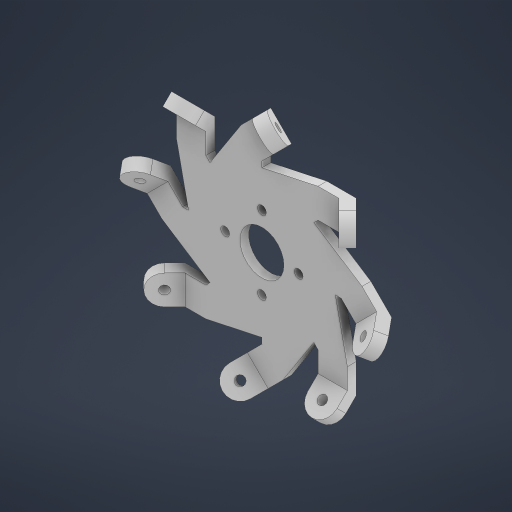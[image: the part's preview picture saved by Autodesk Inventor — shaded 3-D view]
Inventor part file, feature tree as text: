
AUTODESK INVENTOR PART (.ipt)
format: ipt  version: 2023 (Build 270158000, 158)  size: 317,952 bytes
history: native  units: mm
features: extrude x3, sketch x3, plane x1, fillet x1, pattern_circular x1
ambient origin geometry x8: Origin, YZ Plane, XZ Plane, XY Plane, X Axis, Y Axis, Z Axis, Center Point
bodies: Solid1 (feature_tree)
feature tree (9):
  extrude  "Extrusion1"  Depth=50.0mm
  plane  "Work Plane1"
  extrude  "Extrusion2"  Depth=10.0mm
  fillet  "Fillet1"  [1 undecoded]
  extrude  "Extrusion3"  Depth=10.0mm
  pattern_circular  "Circular Pattern1"  Count=8 Angle=360.0deg
  sketch  "Sketch1"  dims[d0=15.0mm d1=50.0mm]
  sketch  "Sketch2"  dims[d3=2.0mm d4=10.0mm d5=135.0deg]
  sketch  "Sketch3"  dims[d6=10.0mm d7=10.0mm d8=80.0mm d10=360.0deg d13=3.0mm d14=3.0mm d15=3.0mm d16=3.0mm d17=3.0mm d18=0.0mm d19=135.0deg d20=10.0mm d21=0.0mm d22=5.0mm d23=3.0mm d24=10.0mm d25=0.0mm d26=80.0mm d27=360.0deg]
note: 1 required parameter value undecoded (feature->parameter linkage not recoverable at this tier; creation-order binding heuristic only, values carry confidence <= 0.55)
